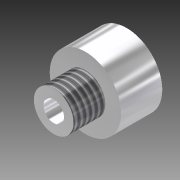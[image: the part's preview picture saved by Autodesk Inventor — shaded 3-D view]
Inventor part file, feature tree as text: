
AUTODESK INVENTOR PART (.ipt)
format: ipt  version: 2011 (Build 150239000, 239)  size: 127,488 bytes
history: native  units: in
note: dims shown in document units (in); Inventor stores cm internally (conversion verified against a paired STEP export)
features: extrude x5, sketch x5, thread x1, plane x1, projected_geometry x1
ambient origin geometry x8: Origin, YZ Plane, XZ Plane, XY Plane, X Axis, Y Axis, Z Axis, Center Point
bodies: Solid1 (feature_tree)
feature tree (13):
  extrude  "Extrusion1"  Depth=0.95in
  extrude  "Extrusion2"  Depth=0.1in TaperAngle=0.0deg
  extrude  "Extrusion3"  Depth=0.5in TaperAngle=0.0deg
  thread  "Thread1"  [1 undecoded]
  plane  "Work Plane1"
  extrude  "Extrusion4"  Depth=0.425in
  extrude  "Extrusion5"  Depth=0.5in TaperAngle=0.0deg
  sketch  "Sketch1"  dims[d0=1.125in d1=0.95in]
  sketch  "Sketch2"  dims[d2=0.55in d3=0.0in d4=0.1in d5=0.0in]
  sketch  "Sketch3"  dims[d6=0.625in d7=0.5in d8=0.0in d9=1.0in d10=0.0in]
  sketch  "Sketch4"  dims[d11=-0.5625in d12=0.425in]
  projected_geometry  "Projected Loop1"
  sketch  "Sketch5"  dims[d13=0.325in d14=0.5in d15=0.0in d16=0.325in d17=0.5in d18=0.0in]
note: 1 required parameter value undecoded (feature->parameter linkage not recoverable at this tier; creation-order binding heuristic only, values carry confidence <= 0.55)
